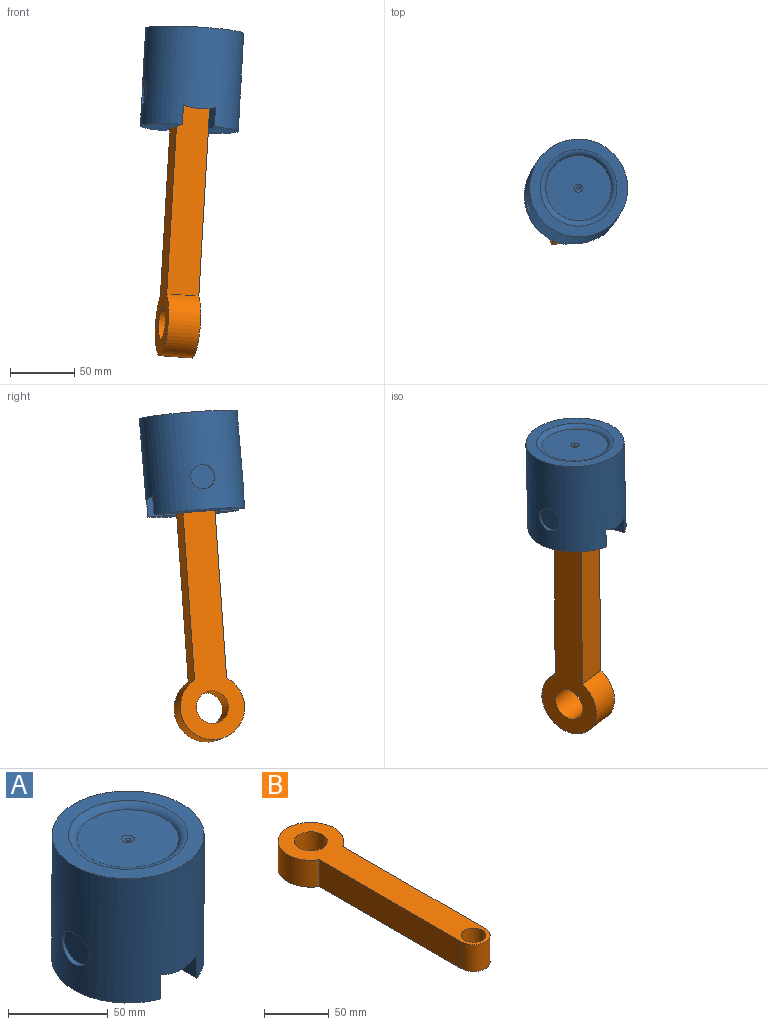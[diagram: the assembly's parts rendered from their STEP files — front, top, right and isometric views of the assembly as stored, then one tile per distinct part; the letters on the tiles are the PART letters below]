
ASSEMBLY  parts=2 mates=1
PART A: 20 faces, bbox 76.2x76.2x76.2 mm
  f0: cylinder r=38.1mm len=76.2mm, axis (0,0,-1), area 16970.8mm2, adj f1,f2,f3,f5,f7,f9,f10,f12
  f1: plane 71.84x25.4mm, normal (0,0,-1), area 1330.7mm2, adj f0,f7
  f2: plane 76.2x76.2mm, normal (0,0,1), area 1770.6mm2, adj f0,f17
  f3: plane 71.84x25.4mm, normal (0,0,-1), area 1330.7mm2, adj f0,f5
  f4: plane 25.4x25.4mm, normal (0,1,0), area 645.2mm2, adj f5,f7,f8,f10
  f5: plane 71.84x50.8mm, normal (-1,0,0), area 2719.4mm2, adj f0,f3,f4,f6,f8,f9,f10,f11
  f6: plane 25.4x25.4mm, normal (0,-1,0), area 645.2mm2, adj f5,f7,f8,f9
  f7: plane 71.84x50.8mm, normal (1,0,0), area 2719.4mm2, adj f0,f1,f4,f6,f8,f9,f10,f11
  f8: plane 50.8x25.4mm, normal (0,0,-1), area 1290.3mm2, adj f4,f5,f6,f7
  f9: plane 25.4x12.7mm, normal (0,-0.71,-0.71), area 430.4mm2, adj f0,f5,f6,f7
  f10: plane 25.4x12.7mm, normal (0,0.71,-0.71), area 430.4mm2, adj f0,f4,f5,f7
  f11: cylinder r=9.53mm len=25.4mm, axis (-1,0,0), area 1520.1mm2, adj f5,f7
  f12: cylinder r=9.53mm len=19.05mm, axis (1,0,0), area 116mm2, adj f0,f13
  f13: plane 19.05x19.05mm, normal (1,0,0), area 285mm2, adj f12
  f14: cylinder r=9.53mm len=19.05mm, axis (-1,0,0), area 116mm2, adj f0,f15
  f15: plane 19.05x19.05mm, normal (-1,0,0), area 285mm2, adj f14
  f16: plane 50.8x50.8mm, normal (0,0,1), area 1995.2mm2, adj f17,f19
  f17: torus R=29.8mm, axis (0,0,1), area 915mm2, adj f2,f16
  f18: plane 2.49x2.49mm, normal (0,0,1), area 4.9mm2, adj f19
  f19: torus R=1.24mm, axis (0,0,-1), area 27.6mm2, adj f16,f18
PART B: 8 faces, bbox 50.8x215.9x25.4 mm
  f0: plane 155.8x25.4mm, normal (-1,0,0), area 3957.4mm2, adj f1,f4,f5,f6
  f1: cylinder r=12.7mm len=25.4mm, axis (0,0,-1), area 1013.4mm2, adj f0,f2,f4,f5
  f2: plane 155.8x25.4mm, normal (1,0,0), area 3957.4mm2, adj f1,f4,f5,f6
  f3: cylinder r=9.53mm len=25.4mm, axis (0,0,-1), area 1520.1mm2, adj f4,f5
  f4: plane 215.9x50.8mm, normal (0,0,1), area 5387.4mm2, adj f0,f1,f2,f3,f6,f7
  f5: plane 215.9x50.8mm, normal (0,0,-1), area 5387.4mm2, adj f0,f1,f2,f3,f6,f7
  f6: cylinder r=25.4mm len=50.8mm, axis (0,0,1), area 3378mm2, adj f0,f2,f4,f5
  f7: cylinder r=12.7mm len=25.4mm, axis (0,0,1), area 2026.8mm2, adj f4,f5
PLACE A rot(axis=(-0.36,0.29,0.89),12.5deg) t=(-156.5,252.35,319.96)mm
PLACE B rot(axis=(-0.67,0.52,-0.52),118.2deg) t=(-167.55,252.05,346.11)mm
MATE revolute B.f1 <-> A.f11  axis (-0.98,-0.19,0.07) through (-155.11,254.47,345.23)mm
